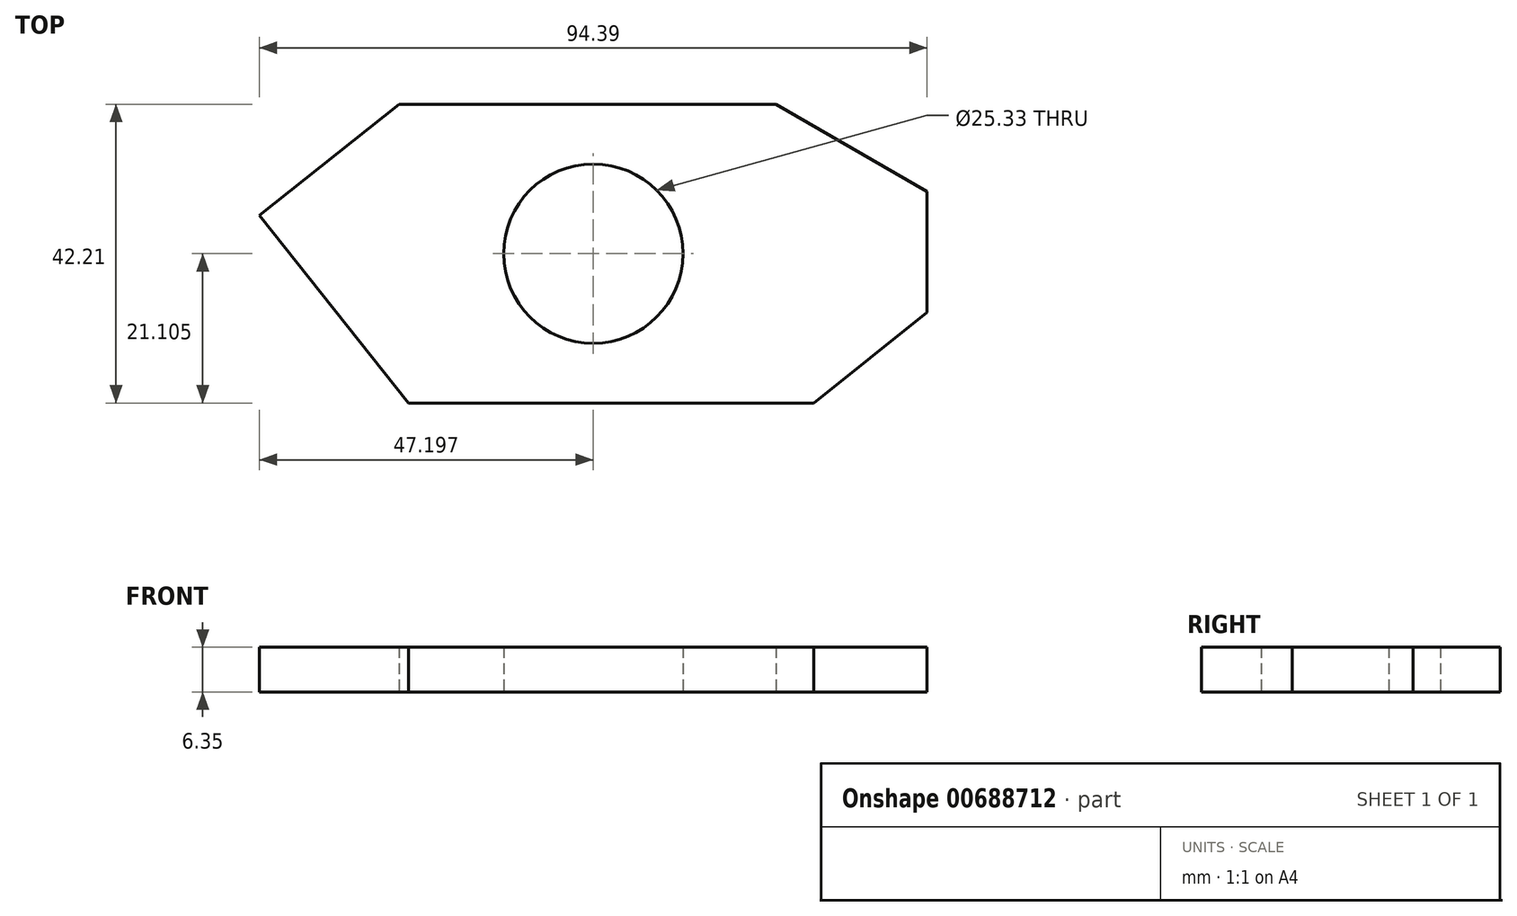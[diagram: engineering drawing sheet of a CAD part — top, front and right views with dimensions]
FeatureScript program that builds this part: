
annotation { "Feature Type Name" : "Feature", "Feature Type Description" : "" }
export const myFeature = defineFeature(function(context is Context, id is Id, definition is map)
    precondition{}
    {
        {
            var Q0;
            Q0=qCreatedBy(makeId("Top.planeOp"),FACE);
            var sketch = newSketch(context, id + "F0", { "sketchPlane" : qUnion([Q0])});
            skLineSegment(sketch, "E0.bottom", {"start": v(-19.63, 29.4) * mm, "end": v(33.64, 29.4) * mm});
            skLineSegment(sketch, "E0.top", {"start": v(-18.24, -12.81) * mm, "end": v(39, -12.81) * mm});
            skLineSegment(sketch, "E0.right", {"start": v(55.03, 17.08) * mm, "end": v(55.03, 0) * mm});
            skCircle(sketch, "E1", {"center": v(7.84, 8.3) * mm, "radius": 12.67 * mm});
            skPoint(sketch, "E1.centerSnap0", {"position": v(55.03, 8.3) * mm});
            skPoint(sketch, "E1.centerSnap1", {"position": v(7.84, 29.4) * mm});
            skLineSegment(sketch, "E2", {"start": v(-19.63, 29.4) * mm, "end": v(-39.36, 13.69) * mm});
            skLineSegment(sketch, "E3", {"start": v(-39.36, 13.69) * mm, "end": v(-18.24, -12.81) * mm});
            skLineSegment(sketch, "E4", {"start": v(33.64, 29.4) * mm, "end": v(55.03, 17.08) * mm});
            skLineSegment(sketch, "E5", {"start": v(55.03, 0) * mm, "end": v(39, -12.81) * mm});
            skPoint(sketch, "E6.orphan", {"position": v(-39.36, 29.4) * mm});
            skPoint(sketch, "E7.orphan", {"position": v(55.03, 29.4) * mm});
            skPoint(sketch, "E8.orphan", {"position": v(55.03, -12.81) * mm});
            skSolve(sketch);
        }
        {
            var Q0;
            Q0=makeQuery(id+"F0.imprint","IMPRINT",FACE,{"disambiguationData":[TD([[makeQuery(id+"F0.imprint","IMPRINT",EDGE,{"derivedFrom":sQuery(id+"F0.wireOp",EDGE,"E0.bottom")}),-1.0]])]});
            extrude(context, id + "F1", {"entities" : qUnion([Q0]), "depth" : 6.35 * mm, "offsetDistance" : 25.4 * mm});
        }
    });
